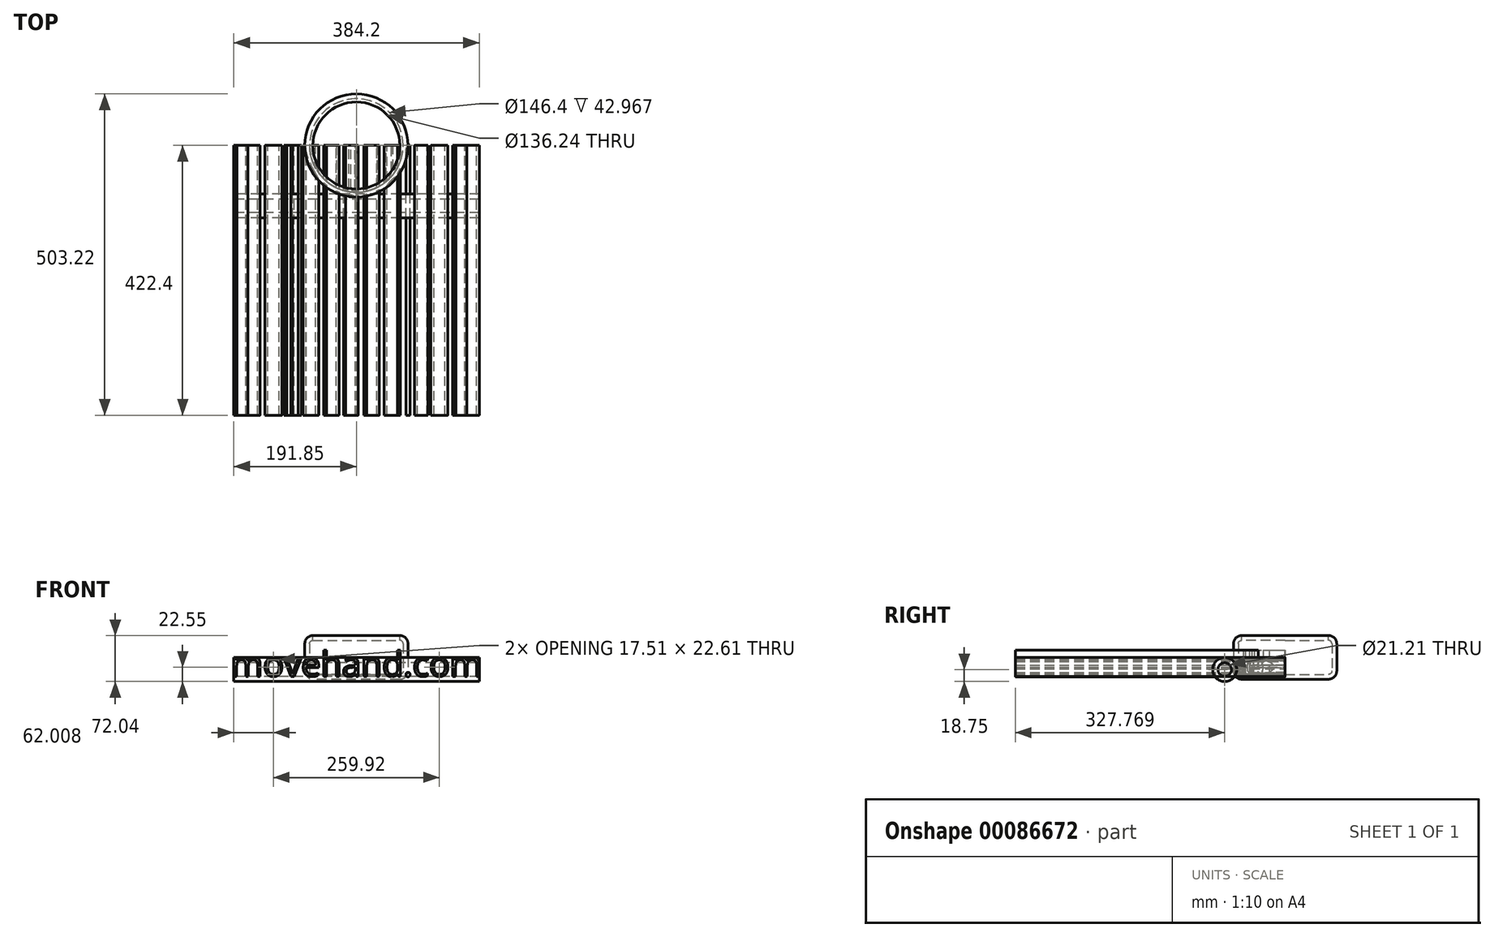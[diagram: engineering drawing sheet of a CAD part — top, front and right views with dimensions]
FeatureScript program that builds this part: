
annotation { "Feature Type Name" : "Feature", "Feature Type Description" : "" }
export const myFeature = defineFeature(function(context is Context, id is Id, definition is map)
    precondition{}
    {
        {
            var Q0;
            Q0=qCreatedBy(makeId("Top.planeOp"),FACE);
            var sketch = newSketch(context, id + "F0", { "sketchPlane" : qUnion([Q0])});
            skCircle(sketch, "E0", {"center": v(0, 0) * mm, "radius": 80.82 * mm});
            skSolve(sketch);
        }
        {
            var Q0;
            Q0=makeQuery(id+"F0.imprint","IMPRINT",FACE,{"disambiguationData":[TD([[makeQuery(id+"F0.imprint","IMPRINT",EDGE,{"derivedFrom":sQuery(id+"F0.wireOp",EDGE,"E0")}),1.0]])]});
            extrude(context, id + "F1", {"entities" : qUnion([Q0]), "depth" : 68.37 * mm});
        }
        {
            var Q0;
            Q0=makeQuery(id+"F1.opExtrude","CAP_EDGE",EDGE,{"disambiguationData":[OSD([sQuery(id+"F0.wireOp",EDGE,"E0")])],"isStart":false});
            var Q1;
            Q1=makeQuery(id+"F1.opExtrude","CAP_EDGE",EDGE,{"disambiguationData":[OSD([sQuery(id+"F0.wireOp",EDGE,"E0")])],"isStart":true});
            var Q2;
            Q2=makeQuery(id+"F1.opExtrude","SWEPT_FACE",FACE,{"disambiguationData":[OSD([sQuery(id+"F0.wireOp",EDGE,"E0")])]});
            fillet(context, id + "F2", {"entities" : qUnion([Q0, Q1, Q2]), "radius" : 12.7 * mm, "tangentPropagation" : true, "allowEdgeOverflow" : false});
        }
        {
            var Q0;
            Q0=makeQuery(id+"F1.opExtrude","CAP_FACE",FACE,{"disambiguationData":[OSD([sQuery(id+"F0.wireOp",EDGE,"E0")])],"isStart":false});
            shell(context, id + "F3", {"entities" : qUnion([Q0]), "thickness" : 7.62 * mm});
        }
        {
            var Q0;
            Q0=qCreatedBy(makeId("Front.planeOp"),FACE);
            var sketch = newSketch(context, id + "F4", { "sketchPlane" : qUnion([Q0])});
            skText(sketch, "E1", { "text": "movehand.com", "fontName": "OpenSans-Regular.ttf"});
            const initialGuessF4  = {"E1": [-0.1965, 0.00443, 1, 0, 0.03895]};
            skSetInitialGuess(sketch, initialGuessF4);
            skSolve(sketch);
        }
        {
            var Q0;
            Q0=makeQuery(id+"F4.imprint","IMPRINT",FACE,{"disambiguationData":[TD([[makeQuery(id+"F4.imprint","IMPRINT",EDGE,{"derivedFrom":sQuery(id+"F4.wireOp",EDGE,"E1.sketch_text.stroke-0")}),-1.0]])]});
            var Q1;
            Q1=makeQuery(id+"F4.imprint","IMPRINT",FACE,{"disambiguationData":[TD([[makeQuery(id+"F4.imprint","IMPRINT",EDGE,{"derivedFrom":sQuery(id+"F4.wireOp",EDGE,"E1.sketch_text.stroke-45")}),-1.0]])]});
            var Q2;
            Q2=makeQuery(id+"F4.imprint","IMPRINT",FACE,{"disambiguationData":[TD([[makeQuery(id+"F4.imprint","IMPRINT",EDGE,{"derivedFrom":sQuery(id+"F4.wireOp",EDGE,"E1.sketch_text.stroke-74")}),-1.0]])]});
            var Q3;
            Q3=makeQuery(id+"F4.imprint","IMPRINT",FACE,{"disambiguationData":[TD([[makeQuery(id+"F4.imprint","IMPRINT",EDGE,{"derivedFrom":sQuery(id+"F4.wireOp",EDGE,"E1.sketch_text.stroke-119")}),-1.0]])]});
            var Q4;
            Q4=makeQuery(id+"F4.imprint","IMPRINT",FACE,{"disambiguationData":[TD([[makeQuery(id+"F4.imprint","IMPRINT",EDGE,{"derivedFrom":sQuery(id+"F4.wireOp",EDGE,"E1.sketch_text.stroke-160")}),-1.0]])]});
            var Q5;
            Q5=makeQuery(id+"F4.imprint","IMPRINT",FACE,{"disambiguationData":[TD([[makeQuery(id+"F4.imprint","IMPRINT",EDGE,{"derivedFrom":sQuery(id+"F4.wireOp",EDGE,"E1.sketch_text.stroke-168")}),-1.0]])]});
            var Q6;
            Q6=makeQuery(id+"F4.imprint","IMPRINT",FACE,{"disambiguationData":[TD([[makeQuery(id+"F4.imprint","IMPRINT",EDGE,{"derivedFrom":sQuery(id+"F4.wireOp",EDGE,"E1.sketch_text.stroke-200")}),-1.0]])]});
            var Q7;
            Q7=makeQuery(id+"F4.imprint","IMPRINT",FACE,{"disambiguationData":[TD([[makeQuery(id+"F4.imprint","IMPRINT",EDGE,{"derivedFrom":sQuery(id+"F4.wireOp",EDGE,"E1.sketch_text.stroke-28")}),-1.0]])]});
            var Q8;
            Q8=makeQuery(id+"F4.imprint","IMPRINT",FACE,{"disambiguationData":[TD([[makeQuery(id+"F4.imprint","IMPRINT",EDGE,{"derivedFrom":sQuery(id+"F4.wireOp",EDGE,"E1.sketch_text.stroke-55")}),-1.0]])]});
            var Q9;
            Q9=makeQuery(id+"F4.imprint","IMPRINT",FACE,{"disambiguationData":[TD([[makeQuery(id+"F4.imprint","IMPRINT",EDGE,{"derivedFrom":sQuery(id+"F4.wireOp",EDGE,"E1.sketch_text.stroke-92")}),-1.0]])]});
            var Q10;
            Q10=makeQuery(id+"F4.imprint","IMPRINT",FACE,{"disambiguationData":[TD([[makeQuery(id+"F4.imprint","IMPRINT",EDGE,{"derivedFrom":sQuery(id+"F4.wireOp",EDGE,"E1.sketch_text.stroke-136")}),-1.0]])]});
            var Q11;
            Q11=makeQuery(id+"F4.imprint","IMPRINT",FACE,{"disambiguationData":[TD([[makeQuery(id+"F4.imprint","IMPRINT",EDGE,{"derivedFrom":sQuery(id+"F4.wireOp",EDGE,"E1.sketch_text.stroke-183")}),-1.0]])]});
            var Q12;
            Q12 = qSketchRegion(id + "F4", true);
            var Q13;
            Q13=makeQuery(id+"F1.opExtrude","SWEPT_FACE",FACE,{"disambiguationData":[OSD([sQuery(id+"F0.wireOp",EDGE,"E0")])]});
            extrude(context, id + "F5", {"entities" : qUnion([Q0, Q1, Q2, Q3, Q4, Q5, Q6, Q7, Q8, Q9, Q10, Q11, Q12]), "operationType" : NewBodyOperationType.ADD, "endBound" : BoundingType.THROUGH_ALL, "endBoundEntityFace" : qUnion([Q13]), "depth" : 25.4 * mm});
        }
        {
            var Q0;
            Q0=makeQuery(id+"F5.opExtrude","SWEPT_FACE",FACE,{"disambiguationData":[OSD([sQuery(id+"F4.wireOp",EDGE,"E1.sketch_text.stroke-14")])]});
            var sketch = newSketch(context, id + "F6", { "sketchPlane" : qUnion([Q0])});
            skCircle(sketch, "E2", {"center": v(94.63, 15.08) * mm, "radius": 18.75 * mm});
            skCircle(sketch, "E3", {"center": v(94.63, 15.08) * mm, "radius": 10.6 * mm});
            skSolve(sketch);
        }
        {
            var Q0;
            Q0=makeQuery(id+"F6.imprint","IMPRINT",FACE,{"disambiguationData":[TD([[makeQuery(id+"F6.imprint","IMPRINT",EDGE,{"derivedFrom":sQuery(id+"F6.wireOp",EDGE,"E3")}),-1.0]])]});
            var Q1;
            {var subQ0=sQuery(id+"F6.wireOp",EDGE,"E2");var subQ1=makeQuery(id+"F5.opExtrude","SWEPT_EDGE",EDGE,{"disambiguationData":[OSD([sQuery(id+"F4.wireOp",EDGE,"E1.sketch_text.stroke-14"),sQuery(id+"F4.wireOp",EDGE,"E1.sketch_text.stroke-15")])]});var subQ2=makeQuery(id+"F6.imprint","INTERSECT",VERTEX,{"disambiguationData":[OD(0.0)],"derivedFrom":[subQ1,subQ0]});Q1=makeQuery(id+"F6.imprint","IMPRINT",FACE,{"disambiguationData":[TD([[makeQuery(id+"F6.imprint","IMPRINT",EDGE,{"disambiguationData":[TD([[subQ2,1.0]])],"derivedFrom":subQ0}),1.0]])]});}
            var Q2;
            {var subQ0=sQuery(id+"F6.wireOp",EDGE,"E2");var subQ1=makeQuery(id+"F5.opExtrude","SWEPT_EDGE",EDGE,{"disambiguationData":[OSD([sQuery(id+"F4.wireOp",EDGE,"E1.sketch_text.stroke-13"),sQuery(id+"F4.wireOp",EDGE,"E1.sketch_text.stroke-14")])]});var subQ2=makeQuery(id+"F6.imprint","INTERSECT",VERTEX,{"disambiguationData":[OD(0.0)],"derivedFrom":[subQ1,subQ0]});Q2=makeQuery(id+"F6.imprint","IMPRINT",FACE,{"disambiguationData":[TD([[makeQuery(id+"F6.imprint","IMPRINT",EDGE,{"disambiguationData":[TD([[subQ2,-1.0]])],"derivedFrom":subQ0}),1.0]])]});}
            var Q3;
            Q3=makeQuery(id+"F5.opExtrude","SWEPT_FACE",FACE,{"disambiguationData":[OSD([sQuery(id+"F4.wireOp",EDGE,"E1.sketch_text.stroke-226")])]});
            extrude(context, id + "F7", {"entities" : qUnion([Q0, Q1, Q2]), "endBound" : BoundingType.UP_TO_SURFACE, "oppositeDirection" : true, "endBoundEntityFace" : qUnion([Q3]), "depth" : 25.4 * mm});
        }
    });
